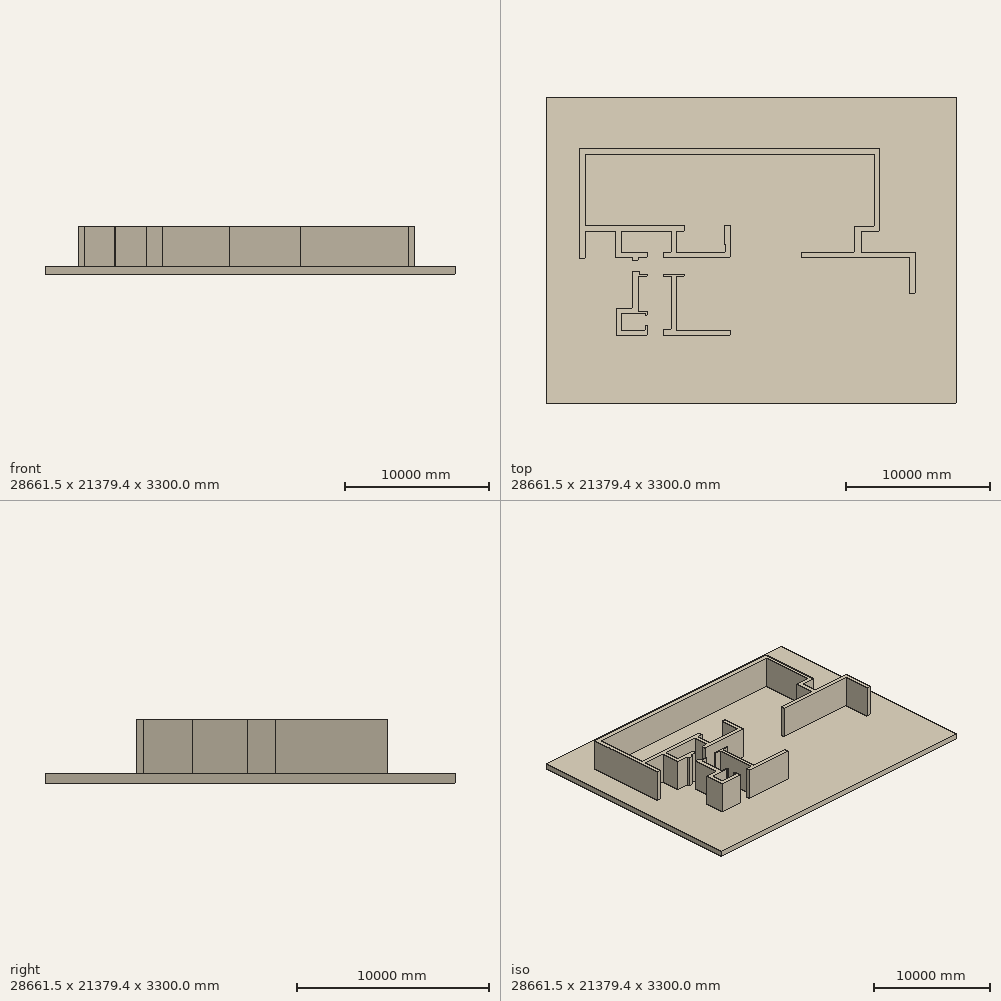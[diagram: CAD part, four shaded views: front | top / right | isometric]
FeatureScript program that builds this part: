
annotation { "Feature Type Name" : "Feature", "Feature Type Description" : "" }
export const myFeature = defineFeature(function(context is Context, id is Id, definition is map)
    precondition{}
    {
        {
            var Q0;
            Q0=qCreatedBy(makeId("Top.planeOp"),FACE);
            var sketch = newSketch(context, id + "F0", { "sketchPlane" : qUnion([Q0])});
            skLineSegment(sketch, "E0", {"start": v(-43.71, 3.77) * mm, "end": v(37.28, 3.77) * mm});
            skLineSegment(sketch, "E1", {"start": v(2323.93, -11149.14) * mm, "end": v(23258.03, -11149.14) * mm});
            skLineSegment(sketch, "E2", {"start": v(23258.03, -11149.14) * mm, "end": v(23258.03, -16950.19) * mm});
            skLineSegment(sketch, "E3", {"start": v(23258.03, -16950.19) * mm, "end": v(21993.47, -16950.19) * mm});
            skLineSegment(sketch, "E4", {"start": v(21993.47, -16950.19) * mm, "end": v(21993.47, -18420.62) * mm});
            skLineSegment(sketch, "E5", {"start": v(21993.47, -18420.62) * mm, "end": v(25815.48, -18420.62) * mm});
            skLineSegment(sketch, "E6", {"start": v(25815.48, -18420.62) * mm, "end": v(25815.48, -24217.8) * mm});
            skLineSegment(sketch, "E7", {"start": v(25815.48, -24217.8) * mm, "end": v(4861.92, -24217.8) * mm});
            skLineSegment(sketch, "E8", {"start": v(4861.92, -24217.8) * mm, "end": v(4861.92, -22304.91) * mm});
            skLineSegment(sketch, "E9", {"start": v(4861.92, -22304.91) * mm, "end": v(6039.48, -22304.91) * mm});
            skLineSegment(sketch, "E10", {"start": v(6039.48, -22304.91) * mm, "end": v(6039.48, -18774.33) * mm});
            skLineSegment(sketch, "E11", {"start": v(6039.48, -18774.33) * mm, "end": v(4852.34, -18774.33) * mm});
            skLineSegment(sketch, "E12", {"start": v(4852.34, -18774.33) * mm, "end": v(4852.34, -16950.19) * mm});
            skLineSegment(sketch, "E13", {"start": v(4852.34, -16950.19) * mm, "end": v(2709.7, -16950.19) * mm});
            skLineSegment(sketch, "E14", {"start": v(2709.7, -16950.19) * mm, "end": v(2709.7, -18803.28) * mm});
            skLineSegment(sketch, "E15", {"start": v(2709.7, -18803.28) * mm, "end": v(2333.29, -18803.28) * mm});
            skLineSegment(sketch, "E16", {"start": v(2333.29, -18803.28) * mm, "end": v(2323.93, -11149.14) * mm});
            skLineSegment(sketch, "E17", {"start": v(2709.7, -11567.18) * mm, "end": v(22895.37, -11542.5) * mm});
            skPoint(sketch, "E17.startSnap0", {"position": v(2709.7, -17876.73) * mm});
            skLineSegment(sketch, "E18", {"start": v(22895.37, -11542.5) * mm, "end": v(22901.5, -16562.78) * mm});
            skLineSegment(sketch, "E19", {"start": v(22901.5, -16562.78) * mm, "end": v(21554.34, -16562.78) * mm});
            skLineSegment(sketch, "E20", {"start": v(21554.34, -16562.78) * mm, "end": v(21556.61, -18420.62) * mm});
            skLineSegment(sketch, "E21", {"start": v(21556.61, -18420.62) * mm, "end": v(17828.2, -18420.62) * mm});
            skLineSegment(sketch, "E22", {"start": v(17828.2, -18420.62) * mm, "end": v(17828.64, -18779.56) * mm});
            skLineSegment(sketch, "E23", {"start": v(17828.64, -18779.56) * mm, "end": v(25402.1, -18779.56) * mm});
            skLineSegment(sketch, "E24", {"start": v(25402.1, -18779.56) * mm, "end": v(25405.2, -21312.9) * mm});
            skLineSegment(sketch, "E25", {"start": v(25405.2, -21312.9) * mm, "end": v(25815.48, -21312.9) * mm});
            skLineSegment(sketch, "E26", {"start": v(12861.96, -24217.8) * mm, "end": v(12861.96, -23846.19) * mm});
            skLineSegment(sketch, "E27", {"start": v(12861.96, -23846.19) * mm, "end": v(9068.9, -23846.19) * mm});
            skLineSegment(sketch, "E28", {"start": v(9068.9, -23846.19) * mm, "end": v(9068.9, -20060.38) * mm});
            skLineSegment(sketch, "E29", {"start": v(9068.9, -20060.38) * mm, "end": v(9662.48, -20060.38) * mm});
            skLineSegment(sketch, "E30", {"start": v(9662.48, -20060.38) * mm, "end": v(9662.48, -19940.94) * mm});
            skLineSegment(sketch, "E31", {"start": v(9662.48, -19940.94) * mm, "end": v(8185.8, -19940.94) * mm});
            skLineSegment(sketch, "E32", {"start": v(8185.8, -19940.94) * mm, "end": v(8185.8, -20064) * mm});
            skLineSegment(sketch, "E33", {"start": v(8185.8, -20064) * mm, "end": v(8764.88, -20064) * mm});
            skLineSegment(sketch, "E34", {"start": v(8764.88, -20064) * mm, "end": v(8764.88, -23817.23) * mm});
            skLineSegment(sketch, "E35", {"start": v(8764.88, -23817.23) * mm, "end": v(8185.8, -23817.23) * mm});
            skLineSegment(sketch, "E36", {"start": v(8185.8, -23817.23) * mm, "end": v(8185.8, -24217.8) * mm});
            skLineSegment(sketch, "E37", {"start": v(7027.6, -24217.8) * mm, "end": v(7027.6, -22528.75) * mm});
            skLineSegment(sketch, "E38", {"start": v(7027.6, -22528.75) * mm, "end": v(6434.04, -22528.75) * mm});
            skLineSegment(sketch, "E39", {"start": v(6434.04, -22528.75) * mm, "end": v(6434.04, -20082.1) * mm});
            skLineSegment(sketch, "E40", {"start": v(6434.04, -20082.1) * mm, "end": v(7042.08, -20082.1) * mm});
            skLineSegment(sketch, "E41", {"start": v(7042.08, -20082.1) * mm, "end": v(7042.08, -19966.27) * mm});
            skLineSegment(sketch, "E42", {"start": v(7042.08, -19966.27) * mm, "end": v(6477.47, -19966.27) * mm});
            skLineSegment(sketch, "E43", {"start": v(6477.47, -19966.27) * mm, "end": v(6477.47, -19749.11) * mm});
            skLineSegment(sketch, "E44", {"start": v(6477.47, -19749.11) * mm, "end": v(6039.48, -19749.11) * mm});
            skLineSegment(sketch, "E45", {"start": v(2709.7, -11567.18) * mm, "end": v(2715.8, -16555.4) * mm});
            skLineSegment(sketch, "E46", {"start": v(2715.8, -16555.4) * mm, "end": v(9645.93, -16546.93) * mm});
            skLineSegment(sketch, "E47", {"start": v(9645.93, -16546.93) * mm, "end": v(9646.4, -16933.94) * mm});
            skLineSegment(sketch, "E48", {"start": v(9646.4, -16933.94) * mm, "end": v(9113.05, -16934.6) * mm});
            skLineSegment(sketch, "E49", {"start": v(9113.05, -16934.6) * mm, "end": v(9114.86, -18414.62) * mm});
            skLineSegment(sketch, "E50", {"start": v(9114.86, -18414.62) * mm, "end": v(12478.97, -18410.5) * mm});
            skLineSegment(sketch, "E51", {"start": v(12478.97, -18410.5) * mm, "end": v(12476.7, -16546.58) * mm});
            skLineSegment(sketch, "E52", {"start": v(12476.7, -16546.58) * mm, "end": v(12866.28, -16546.66) * mm});
            skLineSegment(sketch, "E53", {"start": v(12866.28, -16546.66) * mm, "end": v(12868.99, -18758.8) * mm});
            skLineSegment(sketch, "E54", {"start": v(12868.99, -18758.8) * mm, "end": v(8183.2, -18764.53) * mm});
            skLineSegment(sketch, "E55", {"start": v(8183.2, -18764.53) * mm, "end": v(8182.73, -18380.23) * mm});
            skLineSegment(sketch, "E56", {"start": v(8182.73, -18380.23) * mm, "end": v(8772.2, -18379.51) * mm});
            skLineSegment(sketch, "E57", {"start": v(8772.2, -18379.51) * mm, "end": v(8770.45, -16944.96) * mm});
            skLineSegment(sketch, "E58", {"start": v(8770.45, -16944.96) * mm, "end": v(5225.86, -16949.3) * mm});
            skLineSegment(sketch, "E59", {"start": v(5225.86, -16949.3) * mm, "end": v(5227.64, -18406.7) * mm});
            skLineSegment(sketch, "E60", {"start": v(5227.64, -18406.7) * mm, "end": v(7029.2, -18404.5) * mm});
            skLineSegment(sketch, "E61", {"start": v(7029.2, -18404.5) * mm, "end": v(7029.66, -18778.88) * mm});
            skLineSegment(sketch, "E62", {"start": v(7029.66, -18778.88) * mm, "end": v(6461.78, -18779.57) * mm});
            skLineSegment(sketch, "E63", {"start": v(6461.78, -18779.57) * mm, "end": v(6462.04, -18997.94) * mm});
            skLineSegment(sketch, "E64", {"start": v(6462.04, -18997.94) * mm, "end": v(6039.48, -18998.46) * mm});
            skLineSegment(sketch, "E65", {"start": v(5237.18, -22691.58) * mm, "end": v(6906, -22691.58) * mm});
            skLineSegment(sketch, "E66", {"start": v(6906, -22691.58) * mm, "end": v(6906, -22805.42) * mm});
            skLineSegment(sketch, "E67", {"start": v(6906, -22805.42) * mm, "end": v(7027.6, -22805.42) * mm});
            skLineSegment(sketch, "E68", {"start": v(5237.18, -22691.58) * mm, "end": v(5237.18, -23843.8) * mm});
            skLineSegment(sketch, "E69", {"start": v(5237.18, -23843.8) * mm, "end": v(6909.1, -23843.8) * mm});
            skLineSegment(sketch, "E70", {"start": v(6909.1, -23843.8) * mm, "end": v(6909.1, -23508.74) * mm});
            skLineSegment(sketch, "E71", {"start": v(6909.1, -23508.74) * mm, "end": v(7027.6, -23508.74) * mm});
            skSolve(sketch);
        }
        {
            var Q0;
            Q0=makeQuery(id+"F0.imprint","IMPRINT",FACE,{"disambiguationData":[TD([[makeQuery(id+"F0.imprint","IMPRINT",EDGE,{"derivedFrom":sQuery(id+"F0.wireOp",EDGE,"E1")}),-1.0]])]});
            var Q1;
            {var subQ4=sQuery(id+"F0.wireOp",EDGE,"E8");Q1=makeQuery(id+"F0.imprint","IMPRINT",FACE,{"disambiguationData":[TD([[makeQuery(id+"F0.imprint","IMPRINT",EDGE,{"derivedFrom":subQ4}),-1.0]])]});}
            var Q2;
            {var subQ0=sQuery(id+"F0.wireOp",EDGE,"E26");Q2=makeQuery(id+"F0.imprint","IMPRINT",FACE,{"disambiguationData":[TD([[makeQuery(id+"F0.imprint","IMPRINT",EDGE,{"derivedFrom":subQ0}),1.0]])]});}
            extrude(context, id + "F1", {"entities" : qUnion([Q0, Q1, Q2]), "depth" : 2800 * mm});
        }
        {
            var Q0;
            Q0=qCreatedBy(makeId("Top.planeOp"),FACE);
            var sketch = newSketch(context, id + "F2", { "sketchPlane" : qUnion([Q0])});
            skLineSegment(sketch, "E72.bottom", {"start": v(0, -7583.08) * mm, "end": v(28661.55, -7583.08) * mm});
            skLineSegment(sketch, "E72.top", {"start": v(0, -28962.5) * mm, "end": v(28661.55, -28962.5) * mm});
            skLineSegment(sketch, "E72.left", {"start": v(0, -7583.08) * mm, "end": v(0, -28962.5) * mm});
            skLineSegment(sketch, "E72.right", {"start": v(28661.55, -7583.08) * mm, "end": v(28661.55, -28962.5) * mm});
            skSolve(sketch);
        }
        {
            var Q0;
            Q0=makeQuery(id+"F2.imprint","IMPRINT",FACE,{"disambiguationData":[TD([[makeQuery(id+"F2.imprint","IMPRINT",EDGE,{"derivedFrom":sQuery(id+"F2.wireOp",EDGE,"E72.bottom")}),-1.0]])]});
            extrude(context, id + "F3", {"entities" : qUnion([Q0]), "oppositeDirection" : true, "depth" : 500 * mm});
        }
    });
